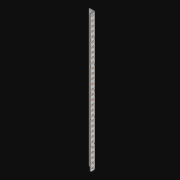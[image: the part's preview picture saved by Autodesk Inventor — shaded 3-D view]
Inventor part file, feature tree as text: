
AUTODESK INVENTOR PART (.ipt)
format: ipt  version: 2021 (Build 250183000, 183)  size: 1,284,608 bytes
history: native  units: in
note: dims shown in document units (in); Inventor stores cm internally (conversion verified against a paired STEP export)
features: extrude x62, other x60, sketch x4, pattern_linear x2, sheet_metal_op x1
ambient origin geometry x8: Origin, YZ Plane, XZ Plane, XY Plane, X Axis, Y Axis, Z Axis, Center Point
bodies: Solid1 (feature_tree)
feature tree (129):
  pattern_linear  "Rectangular Pattern1"  Spacing1=0.5in  [1 undecoded]
  pattern_linear  "Rectangular Pattern3"  Count1=30  [1 undecoded]
  extrude  "Extrusion1"  Depth=0.5in
  extrude  "Extrusion2"  Depth=0.5in
  sketch  "Sketch1"  dims[d0=0.182in]
  other  "Srf1"
  sketch  "Sketch3"  dims[d1=0.063in d2=0.0in]
  other  "Srf3"
  other  "Srf4"
  other  "Srf5"
  other  "Srf6"
  other  "Srf7"
  other  "Srf8"
  other  "Srf9"
  other  "Srf10"
  other  "Srf11"
  other  "Srf12"
  other  "Srf13"
  other  "Srf14"
  other  "Srf15"
  other  "Srf16"
  other  "Srf17"
  other  "Srf18"
  other  "Srf19"
  other  "Srf20"
  other  "Srf21"
  other  "Srf22"
  other  "Srf23"
  other  "Srf24"
  other  "Srf25"
  other  "Srf26"
  other  "Srf27"
  other  "Srf28"
  other  "Srf29"
  other  "Srf30"
  other  "Srf31"
  other  "Srf32"
  other  "Srf142"
  other  "Srf143"
  other  "Srf144"
  other  "Srf145"
  other  "Srf146"
  other  "Srf147"
  other  "Srf148"
  other  "Srf149"
  other  "Srf150"
  other  "Srf151"
  other  "Srf152"
  other  "Srf153"
  other  "Srf154"
  other  "Srf155"
  other  "Srf156"
  other  "Srf157"
  other  "Srf158"
  other  "Srf159"
  other  "Srf160"
  other  "Srf161"
  other  "Srf162"
  other  "Srf163"
  other  "Srf164"
  other  "Srf165"
  other  "Srf166"
  other  "Srf167"
  other  "Srf168"
  other  "Srf169"
  other  "Srf170"
  sketch  "Sketch4"  dims[d6=0.182in]
  sketch  "Sketch5"  dims[d7=0.063in d8=0.0in d11=0.5in d12=0.3937in d14=0.5in d18=11.811in d20=0.5in d21=2.5in d22=0.0in d23=0.841in d24=0.0in]
  sheet_metal_op  "Fold1"
  extrude  "ExtrusionSrf1"  TaperAngle=0.0deg  [1 undecoded]
  extrude  "ExtrusionSrf3"  Depth=0.5in TaperAngle=0.0deg
  extrude  "ExtrusionSrf4"  [1 undecoded]
  extrude  "ExtrusionSrf5"  [1 undecoded]
  extrude  "ExtrusionSrf6"  [1 undecoded]
  extrude  "ExtrusionSrf7"  [1 undecoded]
  extrude  "ExtrusionSrf8"  [1 undecoded]
  extrude  "ExtrusionSrf9"  [1 undecoded]
  extrude  "ExtrusionSrf10"  [1 undecoded]
  extrude  "ExtrusionSrf11"  [1 undecoded]
  extrude  "ExtrusionSrf12"  [1 undecoded]
  extrude  "ExtrusionSrf13"  [1 undecoded]
  extrude  "ExtrusionSrf14"  [1 undecoded]
  extrude  "ExtrusionSrf15"  [1 undecoded]
  extrude  "ExtrusionSrf16"  [1 undecoded]
  extrude  "ExtrusionSrf17"  [1 undecoded]
  extrude  "ExtrusionSrf18"  [1 undecoded]
  extrude  "ExtrusionSrf19"  [1 undecoded]
  extrude  "ExtrusionSrf20"  [1 undecoded]
  extrude  "ExtrusionSrf21"  [1 undecoded]
  extrude  "ExtrusionSrf22"  [1 undecoded]
  extrude  "ExtrusionSrf23"  [1 undecoded]
  extrude  "ExtrusionSrf24"  [1 undecoded]
  extrude  "ExtrusionSrf25"  [1 undecoded]
  extrude  "ExtrusionSrf26"  [1 undecoded]
  extrude  "ExtrusionSrf27"  [1 undecoded]
  extrude  "ExtrusionSrf28"  [1 undecoded]
  extrude  "ExtrusionSrf29"  [1 undecoded]
  extrude  "ExtrusionSrf30"  [1 undecoded]
  extrude  "ExtrusionSrf31"  [1 undecoded]
  extrude  "ExtrusionSrf32"  [1 undecoded]
  extrude  "ExtrusionSrf142"  [1 undecoded]
  extrude  "ExtrusionSrf143"  [1 undecoded]
  extrude  "ExtrusionSrf144"  [1 undecoded]
  extrude  "ExtrusionSrf145"  [1 undecoded]
  extrude  "ExtrusionSrf146"  [1 undecoded]
  extrude  "ExtrusionSrf147"  [1 undecoded]
  extrude  "ExtrusionSrf148"  [1 undecoded]
  extrude  "ExtrusionSrf149"  [1 undecoded]
  extrude  "ExtrusionSrf150"  [1 undecoded]
  extrude  "ExtrusionSrf151"  [1 undecoded]
  extrude  "ExtrusionSrf152"  [1 undecoded]
  extrude  "ExtrusionSrf153"  [1 undecoded]
  extrude  "ExtrusionSrf154"  [1 undecoded]
  extrude  "ExtrusionSrf155"  [1 undecoded]
  extrude  "ExtrusionSrf156"  [1 undecoded]
  extrude  "ExtrusionSrf157"  [1 undecoded]
  extrude  "ExtrusionSrf158"  [1 undecoded]
  extrude  "ExtrusionSrf159"  [1 undecoded]
  extrude  "ExtrusionSrf160"  [1 undecoded]
  extrude  "ExtrusionSrf161"  [1 undecoded]
  extrude  "ExtrusionSrf162"  [1 undecoded]
  extrude  "ExtrusionSrf163"  [1 undecoded]
  extrude  "ExtrusionSrf164"  [1 undecoded]
  extrude  "ExtrusionSrf165"  [1 undecoded]
  extrude  "ExtrusionSrf166"  [1 undecoded]
  extrude  "ExtrusionSrf167"  [1 undecoded]
  extrude  "ExtrusionSrf168"  [1 undecoded]
  extrude  "ExtrusionSrf169"  [1 undecoded]
  extrude  "ExtrusionSrf170"  [1 undecoded]
note: 61 required parameter values undecoded (feature->parameter linkage not recoverable at this tier; creation-order binding heuristic only, values carry confidence <= 0.55)
